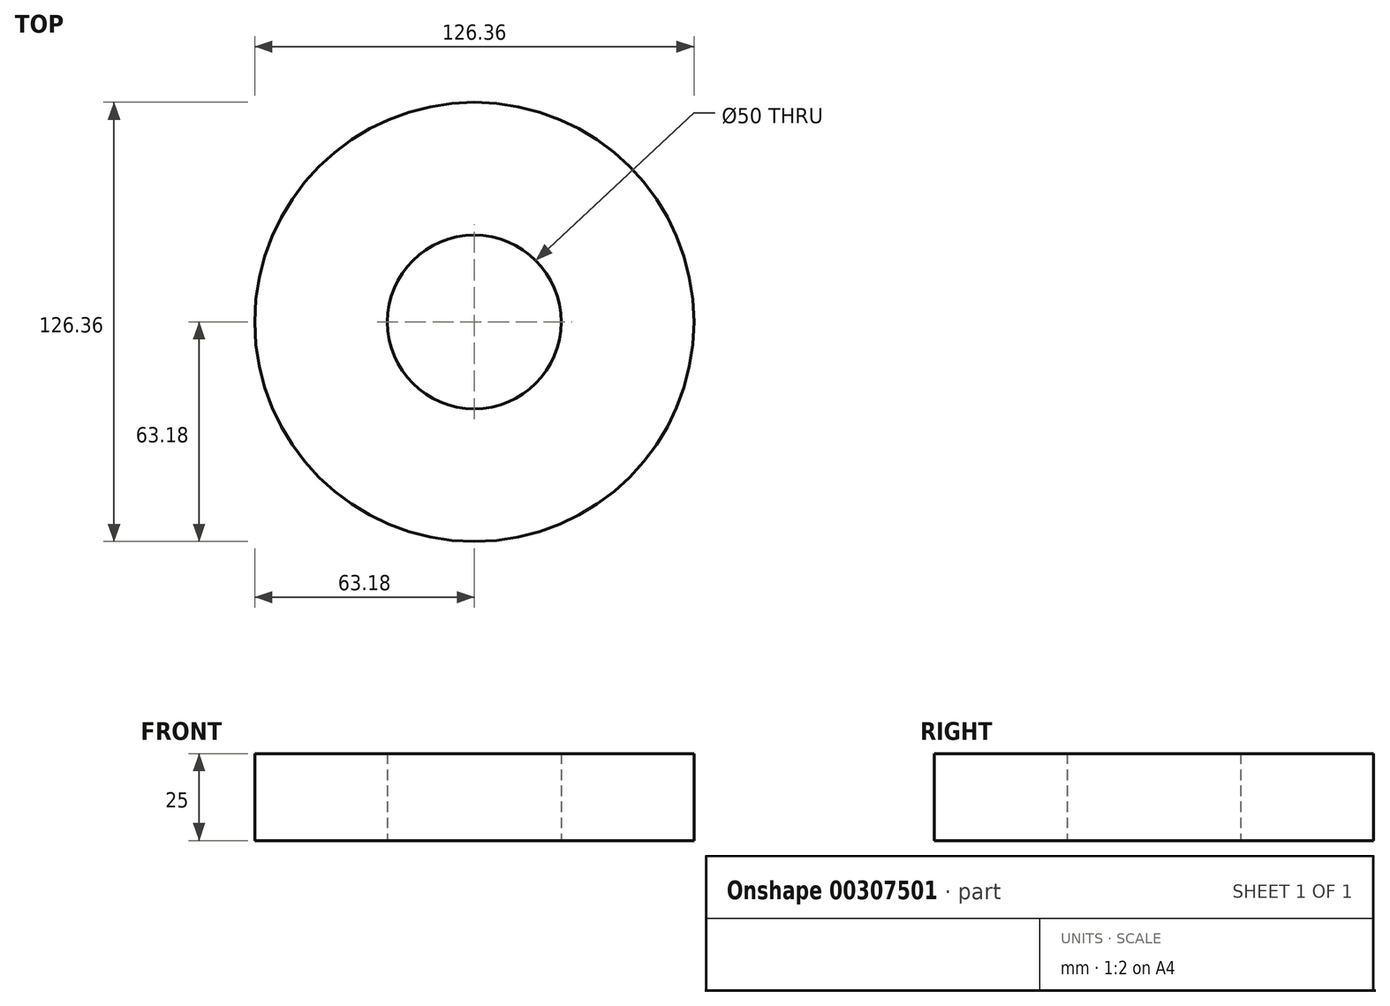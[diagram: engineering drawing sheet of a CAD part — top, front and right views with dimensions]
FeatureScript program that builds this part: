
annotation { "Feature Type Name" : "Feature", "Feature Type Description" : "" }
export const myFeature = defineFeature(function(context is Context, id is Id, definition is map)
    precondition{}
    {
        {
            var Q0;
            Q0=qCreatedBy(makeId("Top.planeOp"),FACE);
            var sketch = newSketch(context, id + "F0", { "sketchPlane" : qUnion([Q0])});
            skCircle(sketch, "E0", {"center": v(0, 0) * mm, "radius": 63.18 * mm});
            skCircle(sketch, "E1", {"center": v(0, 0) * mm, "radius": 25 * mm});
            skSolve(sketch);
        }
        {
            var Q0;
            Q0 = qSketchRegion(id + "F0", true);
            extrude(context, id + "F1", {"entities" : qUnion([Q0]), "depth" : 25 * mm});
        }
    });
